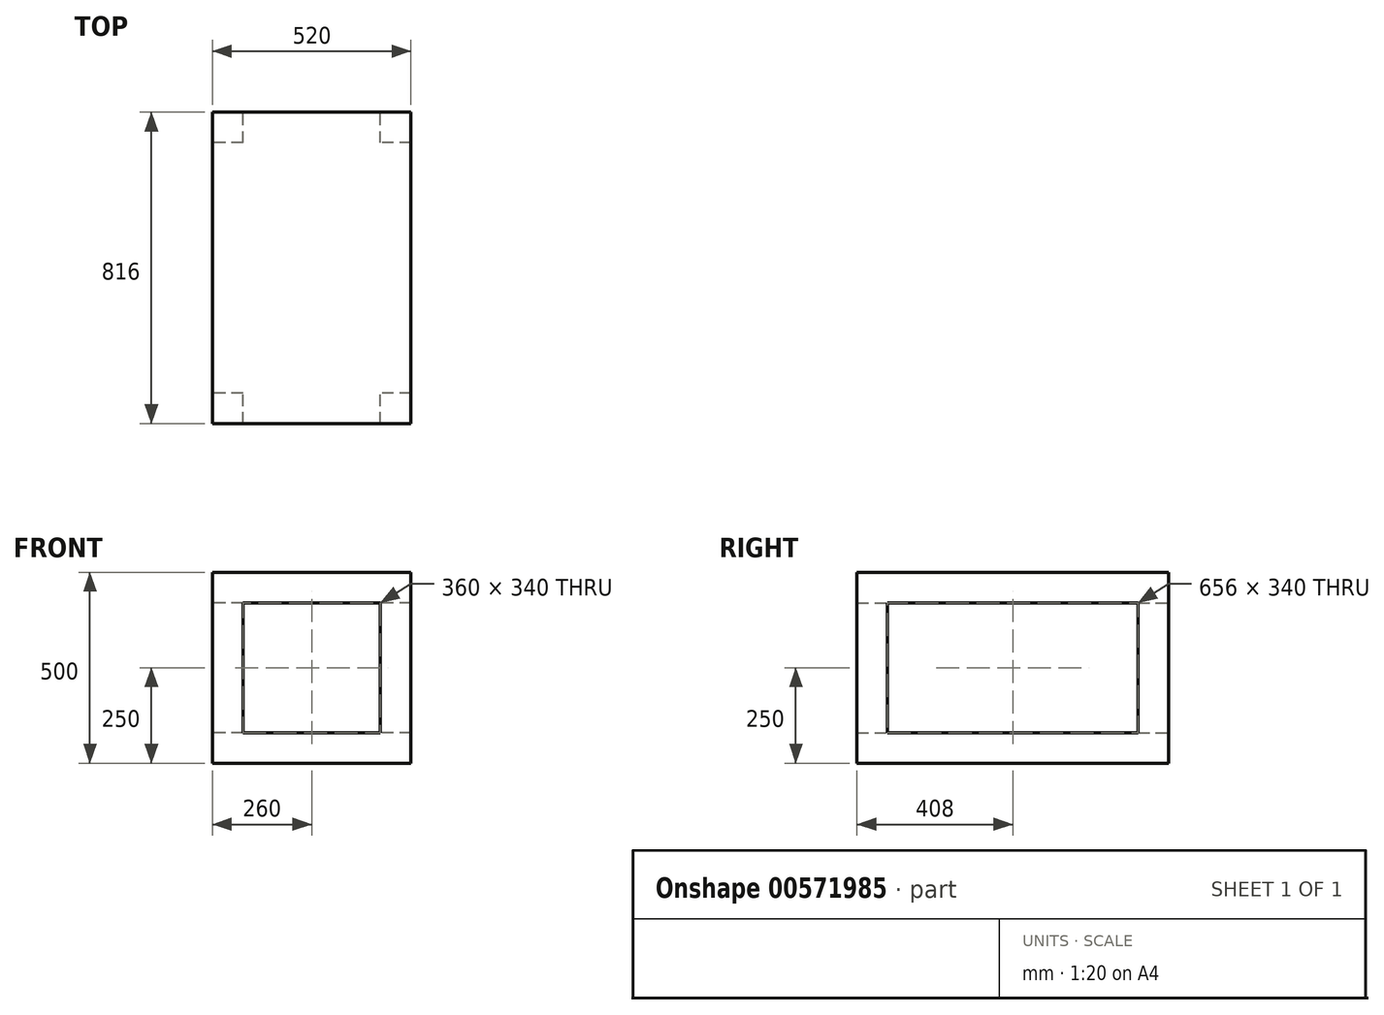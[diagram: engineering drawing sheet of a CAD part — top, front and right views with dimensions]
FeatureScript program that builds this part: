
annotation { "Feature Type Name" : "Feature", "Feature Type Description" : "" }
export const myFeature = defineFeature(function(context is Context, id is Id, definition is map)
    precondition{}
    {
        {
            var Q0;
            Q0=qCreatedBy(makeId("Top.planeOp"),FACE);
            var sketch = newSketch(context, id + "F0", { "sketchPlane" : qUnion([Q0])});
            skLineSegment(sketch, "E0.bottom", {"start": v(260, 408) * mm, "end": v(-260, 408) * mm});
            skLineSegment(sketch, "E0.top", {"start": v(260, -408) * mm, "end": v(-260, -408) * mm});
            skLineSegment(sketch, "E0.left", {"start": v(260, 408) * mm, "end": v(260, -408) * mm});
            skLineSegment(sketch, "E0.right", {"start": v(-260, 408) * mm, "end": v(-260, -408) * mm});
            skPoint(sketch, "E0.middle", {"position": v(0, 0) * mm});
            skSolve(sketch);
        }
        {
            var Q0;
            Q0=makeQuery(id+"F0.imprint","IMPRINT",FACE,{"disambiguationData":[TD([[makeQuery(id+"F0.imprint","IMPRINT",EDGE,{"derivedFrom":sQuery(id+"F0.wireOp",EDGE,"E0.bottom")}),1.0]])]});
            extrude(context, id + "F1", {"entities" : qUnion([Q0]), "depth" : 500 * mm, "offsetDistance" : 25 * mm});
        }
        {
            var Q0;
            Q0=makeQuery(id+"F1.opExtrude","SWEPT_FACE",FACE,{"disambiguationData":[OSD([sQuery(id+"F0.wireOp",EDGE,"E0.bottom")])]});
            var sketch = newSketch(context, id + "F2", { "sketchPlane" : qUnion([Q0])});
            skLineSegment(sketch, "E1.bottom", {"start": v(180, 420) * mm, "end": v(-180, 420) * mm});
            skLineSegment(sketch, "E1.top", {"start": v(180, 80) * mm, "end": v(-180, 80) * mm});
            skLineSegment(sketch, "E1.left", {"start": v(180, 420) * mm, "end": v(180, 80) * mm});
            skLineSegment(sketch, "E1.right", {"start": v(-180, 420) * mm, "end": v(-180, 80) * mm});
            skPoint(sketch, "E1.middle", {"position": v(0, 250) * mm});
            skPoint(sketch, "E1.middle.positionSnap0", {"position": v(260, 250) * mm});
            skPoint(sketch, "E1.centerSnap0", {"position": v(260, 250) * mm});
            skSolve(sketch);
        }
        {
            var Q0;
            Q0 = qSketchRegion(id + "F2", true);
            extrude(context, id + "F3", {"entities" : qUnion([Q0]), "operationType" : NewBodyOperationType.REMOVE, "endBound" : BoundingType.THROUGH_ALL, "oppositeDirection" : true, "depth" : 25 * mm, "offsetDistance" : 25 * mm});
        }
        {
            var Q0;
            Q0=makeQuery(id+"F1.opExtrude","SWEPT_FACE",FACE,{"disambiguationData":[OSD([sQuery(id+"F0.wireOp",EDGE,"E0.right")])]});
            var sketch = newSketch(context, id + "F4", { "sketchPlane" : qUnion([Q0])});
            skLineSegment(sketch, "E2.bottom", {"start": v(328, 420) * mm, "end": v(-328, 420) * mm});
            skLineSegment(sketch, "E2.top", {"start": v(328, 80) * mm, "end": v(-328, 80) * mm});
            skLineSegment(sketch, "E2.left", {"start": v(328, 420) * mm, "end": v(328, 80) * mm});
            skLineSegment(sketch, "E2.right", {"start": v(-328, 420) * mm, "end": v(-328, 80) * mm});
            skPoint(sketch, "E2.middle", {"position": v(0, 250) * mm});
            skPoint(sketch, "E2.middle.positionSnap0", {"position": v(408, 250) * mm});
            skPoint(sketch, "E2.centerSnap0", {"position": v(408, 250) * mm});
            skSolve(sketch);
        }
        {
            var Q0;
            Q0 = qSketchRegion(id + "F4", true);
            extrude(context, id + "F5", {"entities" : qUnion([Q0]), "operationType" : NewBodyOperationType.REMOVE, "endBound" : BoundingType.THROUGH_ALL, "oppositeDirection" : true, "depth" : 25 * mm, "offsetDistance" : 25 * mm});
        }
    });
